# Revit family: LUMINOUS NEON 1217_SLN1217N
name_source: partatom
category: Luminarias
units: mm (PartAtom-declared; Revit-internal decimal feet)

## family parameters
Compartido = No
Corte con vacíos al cargar = No
Cota de conector redondo = Diámetro de uso
Origen de luz = Sí
Punto de cálculo de habitación = No
Se basa en plano de trabajo = Sí
Siempre vertical = No
Tipo de pieza = Normal

## types (3) — shared parameters
Cambio de temperatura de color de luz atenuada = <Ninguno>
Comentarios de vataje = 48V
Fabricante = BRILLANT
Filtro de color = 16777215
Longitud de línea de emisión = 600 mm
Longitud de símbolo de origen de luz = 3048 mm  [stored 10 ft]
Marca = BRILLANT
Modelo Lampara = 1217 NEON
Ángulo de campo de foco = 90.00°
Ángulo de enfoque = 30.00°
Ángulo de inclinación = 60.00°
zero-valued in all types: Elevación por defecto

## per-type parameters (varying)
| type | Descripción | Modelo |
| LUMINOUS NEON 1217_SLN1217N | TIRA LED LUMINOUS NEON 1217 DE SILICONA AMBIENTAL CON UNA POTENCIA DE 5.3W/M, USO PARA EXTERIORES IP67, IRC 90, IK 08, TEMPERATURA DE BLANCO FRIO 4000K, 200 LUMENES/M, PRESENTACION DE 50M, CORTE 10CM, ALIMENTADO A 48V, REQUIERE ACCESORIOS. 36 MIL HORAS DE VIDA. | SLN1217N |
| LUMINOUS NEON 1217_SLN1217W | TIRA LED LUMINOUS NEON 1217 DE SILICONA AMBIENTAL CON UNA POTENCIA DE 5.3W/M, USO PARA EXTERIORES IP67, IRC 90, IK 08, TEMPERATURA DE BLANCO CALIDO 3000K, 200 LUMENES/M, PRESENTACION DE 50M, CORTE 10CM, ALIMENTADO A 48V, REQUIERE ACCESORIOS. 36 MIL HORAS DE VIDA. | SLN1217W |
| LUMINOUS NEON 1217_SLN1217U | TIRA LED LUMINOUS NEON 1217 DE SILICONA AMBIENTAL CON UNA POTENCIA DE 5.3W/M, USO PARA EXTERIORES IP67, IRC 90, IK 08, TEMPERATURA DE BLANCO ULTRA CALIDO 2700K, 200 LUMENES/M, PRESENTACION DE 50M, CORTE 10CM, ALIMENTADO A 48V, REQUIERE ACCESORIOS. 36 MIL HORAS DE VIDA. | SLN1217U |

note: [stored X ft] marks values corroborated as IEEE doubles in the binary element streams (Revit-internal decimal feet)
